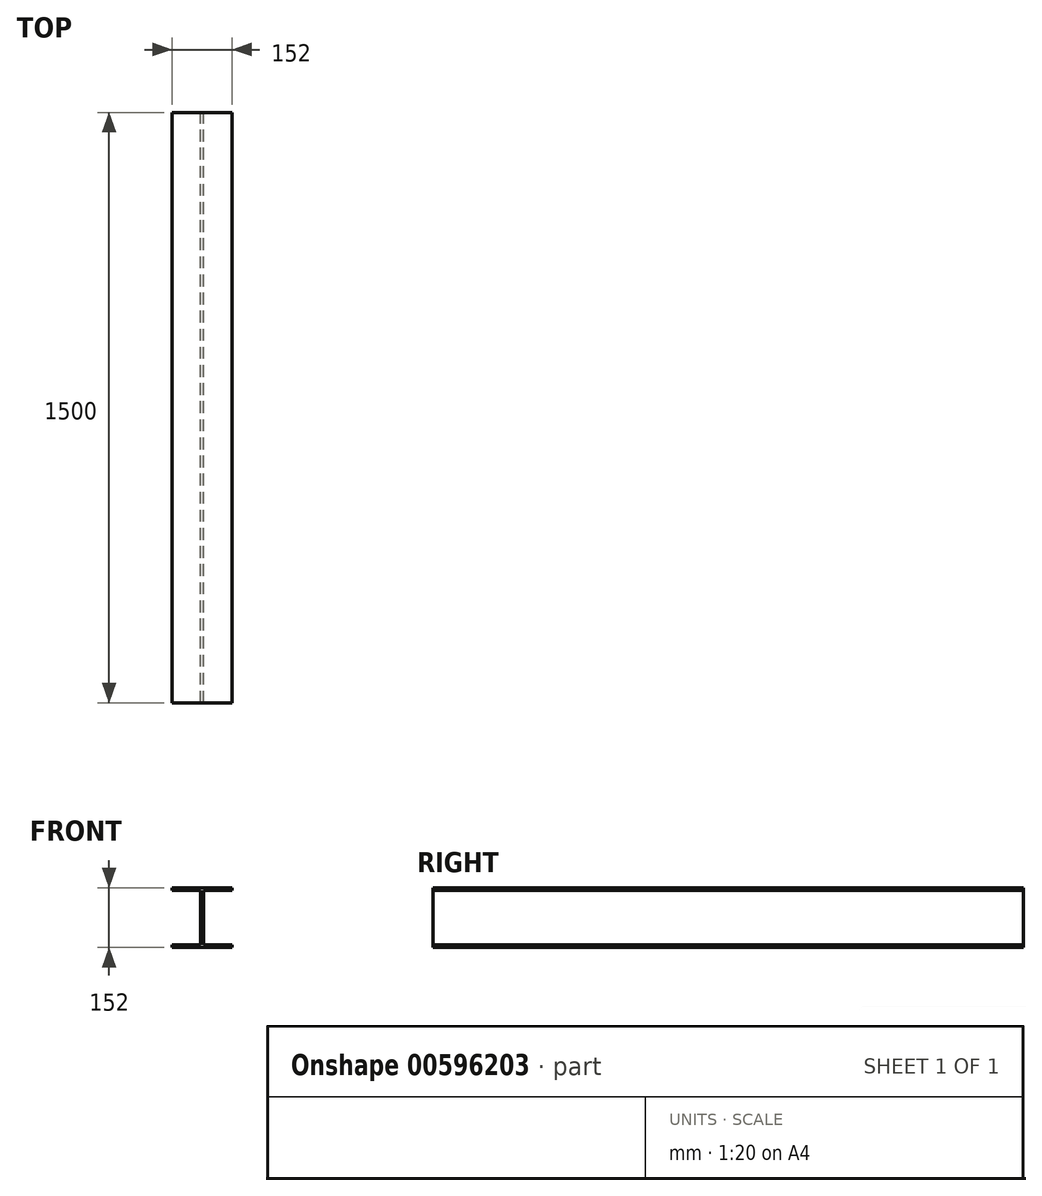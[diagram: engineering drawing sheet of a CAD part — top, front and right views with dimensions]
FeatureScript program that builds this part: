
annotation { "Feature Type Name" : "Feature", "Feature Type Description" : "" }
export const myFeature = defineFeature(function(context is Context, id is Id, definition is map)
    precondition{}
    {
        {
            var Q0;
            Q0=qCreatedBy(makeId("Front.planeOp"),FACE);
            var sketch = newSketch(context, id + "F0", { "sketchPlane" : qUnion([Q0])});
            skLineSegment(sketch, "E0.bottom", {"start": v(-16.45, 118.72) * mm, "end": v(135.55, 118.72) * mm});
            skLineSegment(sketch, "E0.top", {"start": v(-16.45, -33.28) * mm, "end": v(135.55, -33.28) * mm});
            skLineSegment(sketch, "E0.left", {"start": v(-16.45, 118.72) * mm, "end": v(-16.45, -33.28) * mm, "construction": true});
            skLineSegment(sketch, "E0.right", {"start": v(135.55, 118.72) * mm, "end": v(135.55, -33.28) * mm, "construction": true});
            skLineSegment(sketch, "E1", {"start": v(135.55, 112.22) * mm, "end": v(63.05, 112.22) * mm});
            skLineSegment(sketch, "E2", {"start": v(63.05, 112.22) * mm, "end": v(63.05, -26.78) * mm});
            skLineSegment(sketch, "E3", {"start": v(63.05, -26.78) * mm, "end": v(135.55, -26.78) * mm});
            skLineSegment(sketch, "E4", {"start": v(135.55, -26.78) * mm, "end": v(135.55, -33.28) * mm});
            skLineSegment(sketch, "E5", {"start": v(-16.45, -33.28) * mm, "end": v(-16.45, -26.78) * mm});
            skLineSegment(sketch, "E6", {"start": v(-16.45, -26.78) * mm, "end": v(56.05, -26.78) * mm});
            skLineSegment(sketch, "E7", {"start": v(56.05, -26.78) * mm, "end": v(56.05, 112.22) * mm});
            skLineSegment(sketch, "E8", {"start": v(56.05, 112.22) * mm, "end": v(-16.45, 112.22) * mm});
            skLineSegment(sketch, "E9", {"start": v(-16.45, 112.22) * mm, "end": v(-16.45, 118.72) * mm});
            skLineSegment(sketch, "E10", {"start": v(135.55, 112.22) * mm, "end": v(135.55, 118.72) * mm});
            skSolve(sketch);
        }
        {
            var Q0;
            Q0=makeQuery(id+"F0.imprint","IMPRINT",FACE,{"disambiguationData":[TD([[makeQuery(id+"F0.imprint","IMPRINT",EDGE,{"derivedFrom":sQuery(id+"F0.wireOp",EDGE,"E0.top")}),1.0]])]});
            extrude(context, id + "F1", {"entities" : qUnion([Q0]), "depth" : 1500 * mm, "offsetDistance" : 25 * mm});
        }
    });
